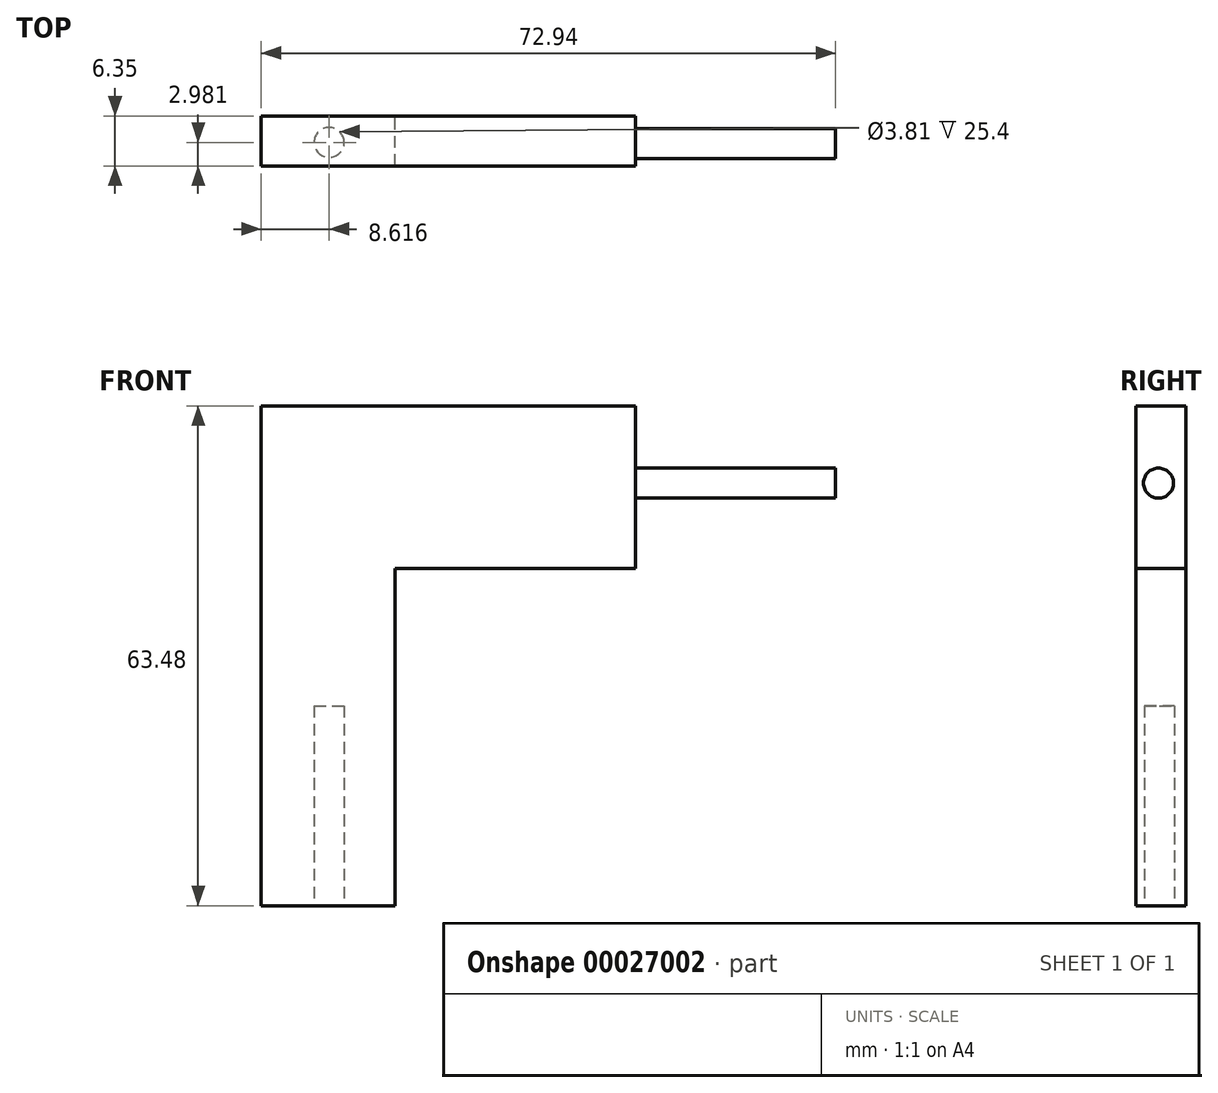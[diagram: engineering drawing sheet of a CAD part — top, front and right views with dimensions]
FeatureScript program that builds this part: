
annotation { "Feature Type Name" : "Feature", "Feature Type Description" : "" }
export const myFeature = defineFeature(function(context is Context, id is Id, definition is map)
    precondition{}
    {
        {
            var Q0;
            Q0=qCreatedBy(makeId("Front.planeOp"),FACE);
            var sketch = newSketch(context, id + "F0", { "sketchPlane" : qUnion([Q0])});
            skLineSegment(sketch, "E0", {"start": v(28.14, 15.88) * mm, "end": v(28.14, -27.57) * mm});
            skLineSegment(sketch, "E1", {"start": v(28.14, -27.57) * mm, "end": v(45.12, -27.57) * mm});
            skLineSegment(sketch, "E2", {"start": v(45.12, -27.57) * mm, "end": v(45.12, 15.24) * mm});
            skLineSegment(sketch, "E3", {"start": v(45.12, 15.24) * mm, "end": v(75.68, 15.24) * mm});
            skLineSegment(sketch, "E4", {"start": v(75.68, 15.24) * mm, "end": v(75.68, 35.91) * mm});
            skLineSegment(sketch, "E5", {"start": v(75.68, 35.91) * mm, "end": v(28.14, 35.91) * mm});
            skLineSegment(sketch, "E6", {"start": v(28.14, 35.91) * mm, "end": v(28.14, 15.88) * mm});
            skSolve(sketch);
        }
        {
            var Q0;
            Q0 = qSketchRegion(id + "F0", true);
            extrude(context, id + "F1", {"entities" : qUnion([Q0]), "depth" : 6.35 * mm});
        }
        {
            var Q0;
            Q0=makeQuery(id+"F1.opExtrude","SWEPT_FACE",FACE,{"disambiguationData":[OSD([sQuery(id+"F0.wireOp",EDGE,"E1")])]});
            var sketch = newSketch(context, id + "F2", { "sketchPlane" : qUnion([Q0])});
            skCircle(sketch, "E7", {"center": v(36.76, 3.37) * mm, "radius": 1.9 * mm});
            skSolve(sketch);
        }
        {
            var Q0;
            Q0=makeQuery(id+"F2.imprint","IMPRINT",FACE,{"disambiguationData":[TD([[makeQuery(id+"F2.imprint","IMPRINT",EDGE,{"derivedFrom":sQuery(id+"F2.wireOp",EDGE,"E7")}),1.0]])]});
            extrude(context, id + "F3", {"entities" : qUnion([Q0]), "operationType" : NewBodyOperationType.REMOVE, "oppositeDirection" : true, "depth" : 25.4 * mm});
        }
        {
            var Q0;
            Q0=makeQuery(id+"F1.opExtrude","SWEPT_FACE",FACE,{"disambiguationData":[OSD([sQuery(id+"F0.wireOp",EDGE,"E4")])]});
            var sketch = newSketch(context, id + "F4", { "sketchPlane" : qUnion([Q0])});
            skCircle(sketch, "E8", {"center": v(-3.5, 26.1) * mm, "radius": 1.9 * mm});
            skSolve(sketch);
        }
        {
            var Q0;
            Q0=makeQuery(id+"F4.imprint","IMPRINT",FACE,{"disambiguationData":[TD([[makeQuery(id+"F4.imprint","IMPRINT",EDGE,{"derivedFrom":sQuery(id+"F4.wireOp",EDGE,"E8")}),1.0]])]});
            var Q1;
            Q1=sQuery(id+"F4.wireOp",EDGE,"E8");
            extrude(context, id + "F5", {"entities" : qUnion([Q0]), "operationType" : NewBodyOperationType.ADD, "surfaceEntities" : qUnion([Q1]), "depth" : 25.4 * mm});
        }
    });
